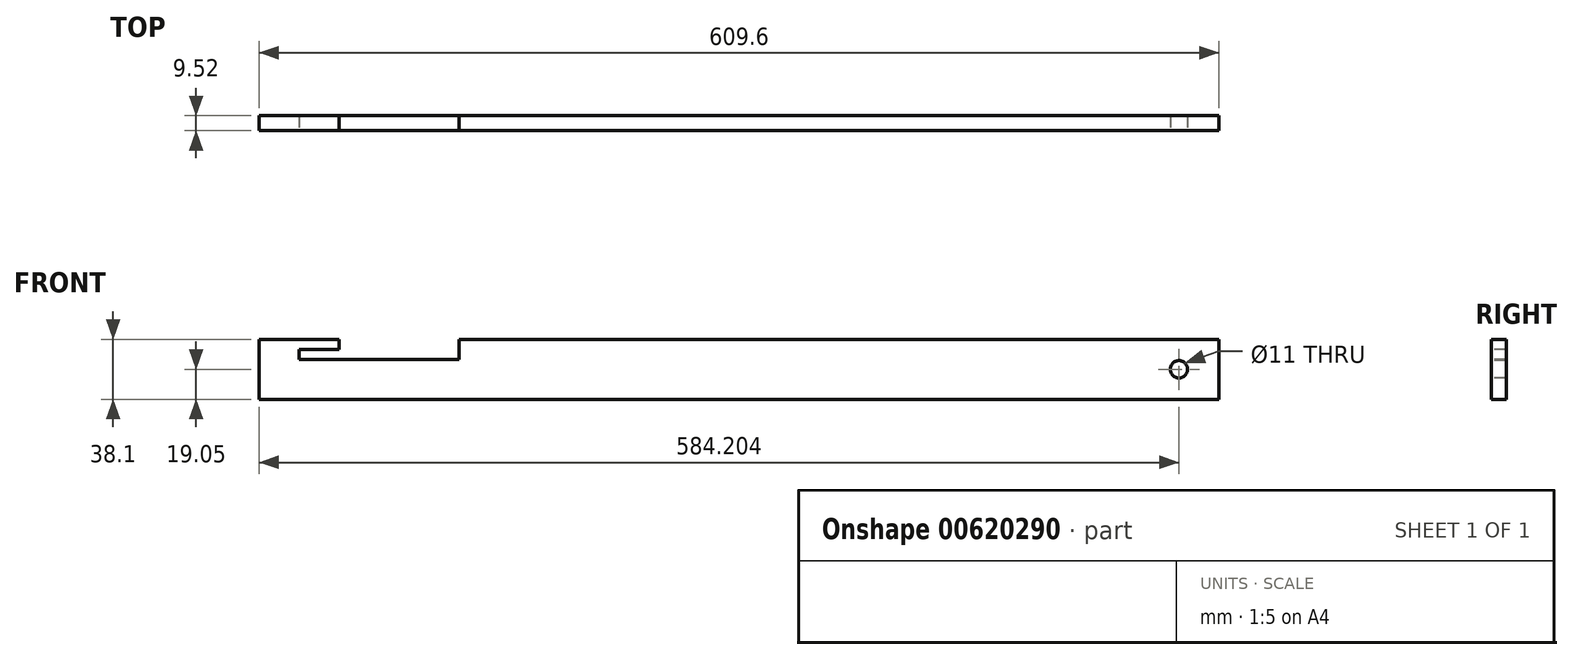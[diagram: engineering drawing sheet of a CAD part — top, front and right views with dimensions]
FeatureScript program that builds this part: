
annotation { "Feature Type Name" : "Feature", "Feature Type Description" : "" }
export const myFeature = defineFeature(function(context is Context, id is Id, definition is map)
    precondition{}
    {
        {
            var Q0;
            Q0=qCreatedBy(makeId("Top.planeOp"),FACE);
            var sketch = newSketch(context, id + "F0", { "sketchPlane" : qUnion([Q0])});
            skLineSegment(sketch, "E0.bottom", {"start": v(47.68, 8.74) * mm, "end": v(-53.92, 8.74) * mm});
            skLineSegment(sketch, "E0.top", {"start": v(47.68, -35.71) * mm, "end": v(-53.92, -35.71) * mm});
            skLineSegment(sketch, "E0.left", {"start": v(47.68, 8.74) * mm, "end": v(47.68, -35.71) * mm});
            skLineSegment(sketch, "E0.right", {"start": v(-53.92, 8.74) * mm, "end": v(-53.92, -35.71) * mm});
            skSolve(sketch);
        }
        {
            var Q0;
            Q0=qSketchRegion(id+"F0",true);
            extrude(context, id + "F1", {"entities" : qUnion([Q0]), "depth" : 6.35 * mm, "offsetDistance" : 25.4 * mm});
        }
        {
            var Q0;
            Q0=makeQuery(id+"F1.opExtrude","SWEPT_FACE",FACE,{"disambiguationData":[OSD([sQuery(id+"F0.wireOp",EDGE,"E0.top")])]});
            var sketch = newSketch(context, id + "F2", { "sketchPlane" : qUnion([Q0])});
            skLineSegment(sketch, "E1.bottom", {"start": v(-79.32, 12.7) * mm, "end": v(530.28, 12.7) * mm});
            skLineSegment(sketch, "E1.top", {"start": v(-79.32, -25.4) * mm, "end": v(530.28, -25.4) * mm});
            skLineSegment(sketch, "E1.left", {"start": v(-79.32, 12.7) * mm, "end": v(-79.32, -25.4) * mm});
            skLineSegment(sketch, "E1.right", {"start": v(530.28, 12.7) * mm, "end": v(530.28, -25.4) * mm});
            skLineSegment(sketch, "E2.bottom", {"start": v(47.68, 6.35) * mm, "end": v(-53.92, 6.35) * mm});
            skLineSegment(sketch, "E2.top", {"start": v(47.68, 0) * mm, "end": v(-53.92, 0) * mm});
            skLineSegment(sketch, "E2.left", {"start": v(47.68, 6.35) * mm, "end": v(47.68, 0) * mm});
            skLineSegment(sketch, "E2.right", {"start": v(-53.92, 6.35) * mm, "end": v(-53.92, 0) * mm});
            skSolve(sketch);
        }
        {
            var Q0;
            Q0 = qSketchRegion(id + "F2", true);
            extrude(context, id + "F3", {"entities" : qUnion([Q0]), "oppositeDirection" : true, "depth" : 9.52 * mm, "offsetDistance" : 25.4 * mm});
        }
        {
            var Q0;
            Q0=makeQuery(id+"F2.imprint","IMPRINT",FACE,{"disambiguationData":[TD([[makeQuery(id+"F2.imprint","IMPRINT",EDGE,{"derivedFrom":sQuery(id+"F2.wireOp",EDGE,"E2.bottom")}),1.0]])]});
            extrude(context, id + "F4", {"entities" : qUnion([Q0]), "operationType" : NewBodyOperationType.REMOVE, "oppositeDirection" : true, "depth" : 9.52 * mm, "offsetDistance" : 25.4 * mm});
        }
        {
            var Q0;
            Q0=makeQuery(id+"F1.opExtrude","SWEPT_BODY",BODY,{"disambiguationData":[OSD([sQuery(id+"F0.wireOp",EDGE,"E0.bottom"),sQuery(id+"F0.wireOp",EDGE,"E0.top"),sQuery(id+"F0.wireOp",EDGE,"E0.left"),sQuery(id+"F0.wireOp",EDGE,"E0.right")])]});
            deleteBodies(context, id + "F5", {"entities" : qUnion([Q0])});
        }
        {
            var Q0;
            Q0=makeQuery(id+"F3.opExtrude","CAP_FACE",FACE,{"disambiguationData":[OSD([sQuery(id+"F2.wireOp",EDGE,"E1.bottom"),sQuery(id+"F2.wireOp",EDGE,"E1.top"),sQuery(id+"F2.wireOp",EDGE,"E1.left"),sQuery(id+"F2.wireOp",EDGE,"E1.right"),sQuery(id+"F2.wireOp",EDGE,"E2.bottom"),sQuery(id+"F2.wireOp",EDGE,"E2.top"),sQuery(id+"F2.wireOp",EDGE,"E2.left"),sQuery(id+"F2.wireOp",EDGE,"E2.right")])],"isStart":true});
            var sketch = newSketch(context, id + "F6", { "sketchPlane" : qUnion([Q0])});
            skLineSegment(sketch, "E3.bottom", {"start": v(47.68, 31.75) * mm, "end": v(-28.52, 31.75) * mm});
            skLineSegment(sketch, "E3.top", {"start": v(47.68, 6.35) * mm, "end": v(-28.52, 6.35) * mm});
            skLineSegment(sketch, "E3.left", {"start": v(47.68, 31.75) * mm, "end": v(47.68, 6.35) * mm});
            skLineSegment(sketch, "E4.0", {"start": v(-28.52, 31.75) * mm, "end": v(-28.52, 6.35) * mm});
            skSolve(sketch);
        }
        {
            var Q0;
            Q0 = qSketchRegion(id + "F6", true);
            extrude(context, id + "F7", {"entities" : qUnion([Q0]), "operationType" : NewBodyOperationType.REMOVE, "oppositeDirection" : true, "depth" : 25.4 * mm, "offsetDistance" : 25.4 * mm});
        }
        {
            var Q0;
            Q0=makeQuery(id+"F3.opExtrude","CAP_FACE",FACE,{"disambiguationData":[OSD([sQuery(id+"F2.wireOp",EDGE,"E1.bottom"),sQuery(id+"F2.wireOp",EDGE,"E1.top"),sQuery(id+"F2.wireOp",EDGE,"E1.left"),sQuery(id+"F2.wireOp",EDGE,"E1.right"),sQuery(id+"F2.wireOp",EDGE,"E2.bottom"),sQuery(id+"F2.wireOp",EDGE,"E2.top"),sQuery(id+"F2.wireOp",EDGE,"E2.left"),sQuery(id+"F2.wireOp",EDGE,"E2.right")])],"isStart":true});
            var sketch = newSketch(context, id + "F8", { "sketchPlane" : qUnion([Q0])});
            skCircle(sketch, "E5", {"center": v(504.88, -6.35) * mm, "radius": 5.5 * mm});
            skSolve(sketch);
        }
        {
            var Q0;
            Q0 = qSketchRegion(id + "F8", true);
            extrude(context, id + "F9", {"entities" : qUnion([Q0]), "operationType" : NewBodyOperationType.REMOVE, "oppositeDirection" : true, "depth" : 25.4 * mm, "offsetDistance" : 25.4 * mm});
        }
    });
